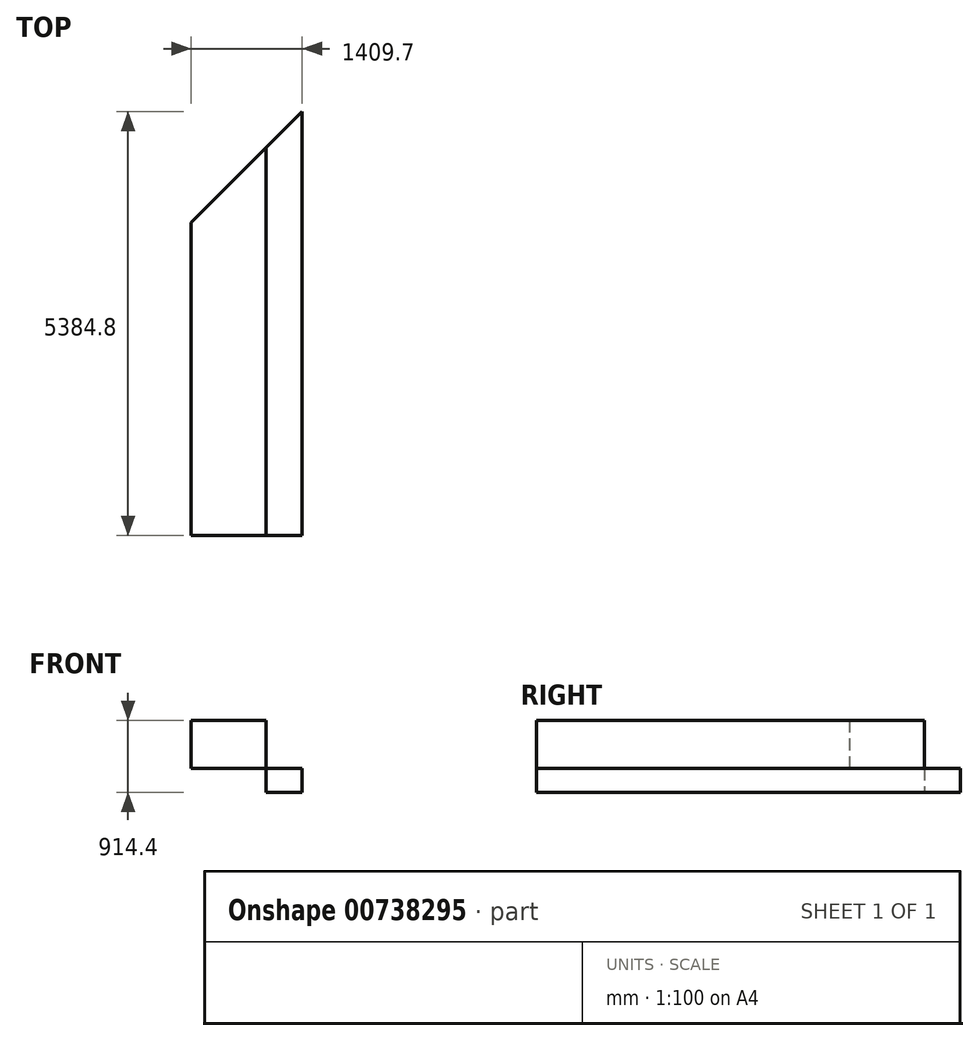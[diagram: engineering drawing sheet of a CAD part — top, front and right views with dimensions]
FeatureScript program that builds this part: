
annotation { "Feature Type Name" : "Feature", "Feature Type Description" : "" }
export const myFeature = defineFeature(function(context is Context, id is Id, definition is map)
    precondition{}
    {
        {
            var Q0;
            Q0=qCreatedBy(makeId("Front.planeOp"),FACE);
            var sketch = newSketch(context, id + "F0", { "sketchPlane" : qUnion([Q0])});
            skLineSegment(sketch, "E0.bottom", {"start": v(0, 220.76) * mm, "end": v(457.2, 220.76) * mm});
            skLineSegment(sketch, "E0.top", {"start": v(0, -84.04) * mm, "end": v(457.2, -84.04) * mm});
            skLineSegment(sketch, "E0.left", {"start": v(0, 220.76) * mm, "end": v(0, -84.04) * mm});
            skLineSegment(sketch, "E0.right", {"start": v(457.2, 220.76) * mm, "end": v(457.2, -84.04) * mm});
            skPoint(sketch, "E0.middle", {"position": v(228.6, 68.36) * mm});
            skSolve(sketch);
        }
        {
            var Q0;
            Q0=makeQuery(id+"F0.imprint","IMPRINT",FACE,{"disambiguationData":[TD([[makeQuery(id+"F0.imprint","IMPRINT",EDGE,{"derivedFrom":sQuery(id+"F0.wireOp",EDGE,"E0.bottom")}),-1.0]])]});
            var sketch = newSketch(context, id + "F1", { "sketchPlane" : qUnion([Q0])});
            skLineSegment(sketch, "E1", {"start": v(0, 220.76) * mm, "end": v(0, 830.36) * mm});
            skLineSegment(sketch, "E2", {"start": v(0, 830.36) * mm, "end": v(-952.5, 830.36) * mm});
            skLineSegment(sketch, "E3", {"start": v(-952.5, 830.36) * mm, "end": v(-952.5, 220.76) * mm});
            skLineSegment(sketch, "E4", {"start": v(-952.5, 220.76) * mm, "end": v(0, 220.76) * mm});
            skSolve(sketch);
        }
        {
            var Q0;
            Q0 = qSketchRegion(id + "F0", true);
            extrude(context, id + "F2", {"entities" : qUnion([Q0]), "oppositeDirection" : true, "depth" : 5410.2 * mm, "offsetDistance" : 25.4 * mm});
        }
        {
            var Q0;
            Q0 = qSketchRegion(id + "F1", true);
            extrude(context, id + "F3", {"entities" : qUnion([Q0]), "oppositeDirection" : true, "depth" : 4927.6 * mm, "offsetDistance" : 25.4 * mm});
        }
        {
            var Q0;
            Q0=makeQuery(id+"F2.opExtrude","CAP_EDGE",EDGE,{"disambiguationData":[OSD([sQuery(id+"F0.wireOp",EDGE,"E0.left")])],"isStart":false});
            chamfer(context, id + "F4", {"entities" : qUnion([Q0]), "width" : 482.6 * mm, "tangentPropagation" : true});
        }
        {
            var Q0;
            Q0=makeQuery(id+"F3.opExtrude","CAP_EDGE",EDGE,{"disambiguationData":[OSD([sQuery(id+"F1.wireOp",EDGE,"E3")])],"isStart":false});
            chamfer(context, id + "F5", {"entities" : qUnion([Q0]), "width" : 952.5 * mm, "tangentPropagation" : true});
        }
    });
